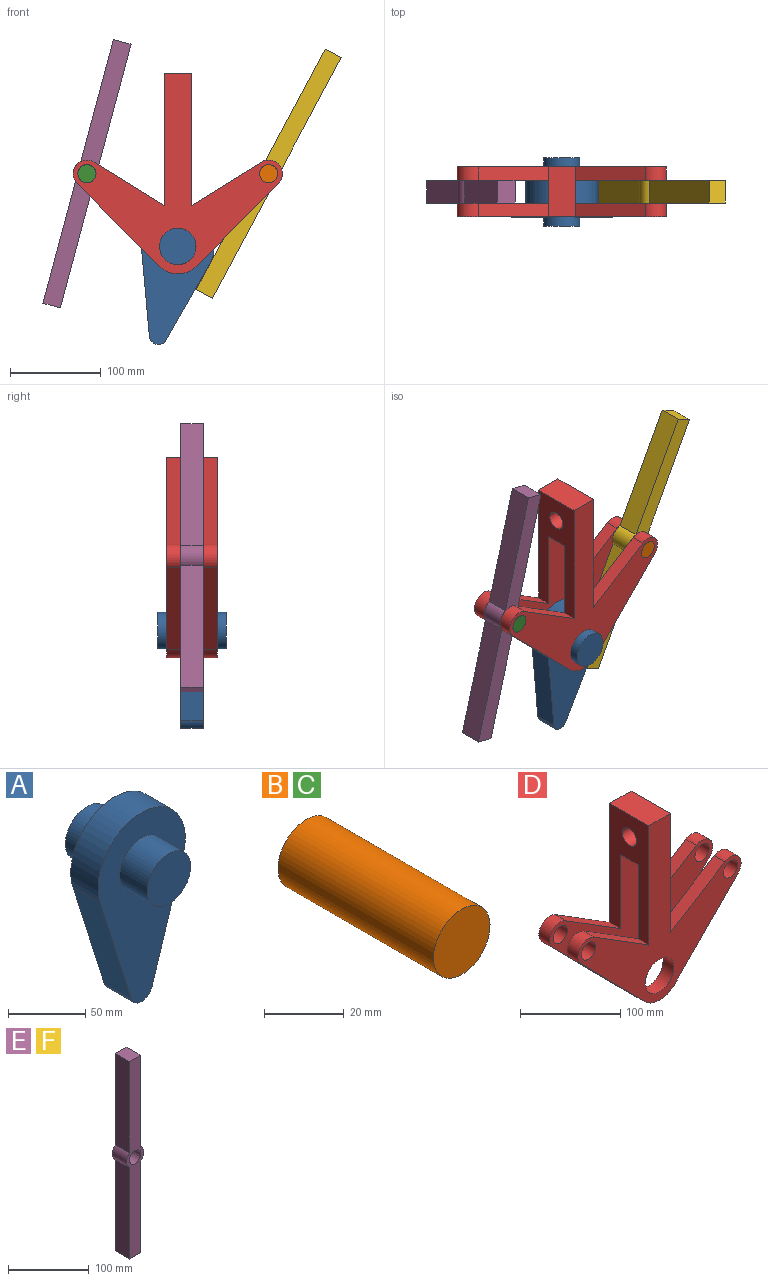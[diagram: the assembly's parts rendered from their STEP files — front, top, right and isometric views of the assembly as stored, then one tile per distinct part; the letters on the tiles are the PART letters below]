
ASSEMBLY  parts=6 mates=5
PART A: 10 faces, bbox 80x75x150 mm
  f0: cylinder r=10mm len=25mm, axis (0,1,0), area 633.1mm2, adj f1,f3,f4,f5
  f1: plane 91x28.62mm, normal (0.95,0,-0.3), area 2384.8mm2, adj f0,f2,f4,f5
  f2: cylinder r=40mm len=80mm, axis (0,1,0), area 3751mm2, adj f1,f3,f4,f5
  f3: plane 91x28.62mm, normal (-0.95,0,-0.3), area 2384.8mm2, adj f0,f2,f4,f5
  f4: plane 150x80mm, normal (0,-1,0), area 6640.5mm2, adj f0,f1,f2,f3,f8
  f5: plane 150x80mm, normal (0,1,0), area 6640.5mm2, adj f0,f1,f2,f3,f7
  f6: plane 40x40mm, normal (0,1,0), area 1256.6mm2, adj f7
  f7: cylinder r=20mm len=40mm, axis (0,1,0), area 3141.6mm2, adj f5,f6
  f8: cylinder r=20mm len=40mm, axis (0,1,0), area 3141.6mm2, adj f4,f9
  f9: plane 40x40mm, normal (0,-1,0), area 1256.6mm2, adj f8
PART B: 3 faces, bbox 20x55x20 mm
  f0: cylinder r=10mm len=55mm, axis (0,1,0), area 3455.8mm2, adj f1,f2
  f1: plane 20x20mm, normal (0,-1,0), area 314.2mm2, adj f0
  f2: plane 20x20mm, normal (0,1,0), area 314.2mm2, adj f0
PART C: same geometry as B
PART D: 29 faces, bbox 229.7x55x220 mm
  f0: plane 90.45x89.19mm, normal (-0.71,0,-0.7), area 1905.4mm2, adj f2,f20,f23,f26
  f1: plane 90.45x89.19mm, normal (-0.71,0,-0.7), area 1905.4mm2, adj f3,f21,f24,f27
  f2: cylinder r=30mm len=42.72mm, axis (0,1,0), area 713.2mm2, adj f0,f4,f23,f26
  f3: cylinder r=30mm len=42.72mm, axis (0,1,0), area 713.2mm2, adj f1,f5,f24,f27
  f4: plane 90.45x89.19mm, normal (0.71,0,-0.7), area 1905.4mm2, adj f2,f6,f23,f26
  f5: plane 90.45x89.19mm, normal (0.71,0,-0.7), area 1905.4mm2, adj f3,f7,f24,f27
  f6: cylinder r=15mm len=25.53mm, axis (0,1,0), area 654mm2, adj f4,f8,f23,f26
  f7: cylinder r=15mm len=25.53mm, axis (0,1,0), area 654mm2, adj f5,f9,f24,f27
  f8: plane 76.93x47.95mm, normal (-0.53,0,0.85), area 1359.8mm2, adj f6,f10,f23,f26
  f9: plane 76.93x47.95mm, normal (-0.53,0,0.85), area 1359.8mm2, adj f7,f10,f24,f27
  f10: plane 145.3x55mm, normal (1,0,0), area 5419.9mm2, adj f8,f9,f22,f23,f24,f25,f26,f27
  f11: plane 145.3x55mm, normal (-1,0,0), area 5419.9mm2, adj f12,f13,f22,f23,f24,f25,f26,f27
  f12: plane 76.93x47.95mm, normal (0.53,0,0.85), area 1359.8mm2, adj f11,f20,f23,f26
  f13: plane 76.93x47.95mm, normal (0.53,0,0.85), area 1359.8mm2, adj f11,f21,f24,f27
  f14: cylinder r=20mm len=40mm, axis (0,1,0), area 1885mm2, adj f23,f26
  f15: cylinder r=20mm len=40mm, axis (0,1,0), area 1885mm2, adj f24,f27
  f16: cylinder r=10mm len=20mm, axis (0,1,0), area 942.5mm2, adj f23,f26
  f17: cylinder r=10mm len=20mm, axis (0,1,0), area 942.5mm2, adj f24,f27
  f18: cylinder r=10mm len=20mm, axis (0,1,0), area 942.5mm2, adj f23,f26
  f19: cylinder r=10mm len=20mm, axis (0,1,0), area 942.5mm2, adj f24,f27
  f20: cylinder r=15mm len=25.53mm, axis (0,1,0), area 654mm2, adj f0,f12,f23,f26
  f21: cylinder r=15mm len=25.53mm, axis (0,1,0), area 654mm2, adj f1,f13,f24,f27
  f22: plane 55x30mm, normal (0,0,1), area 1650mm2, adj f10,f11,f23,f24
  f23: plane 229.74x220mm, normal (0,-1,0), area 14852.9mm2, adj f0,f2,f4,f6,f8,f10,f11,f12
  f24: plane 229.74x220mm, normal (0,1,0), area 14852.9mm2, adj f1,f3,f5,f7,f9,f10,f11,f13
  f25: cylinder r=10mm len=30mm, axis (-1,0,0), area 1885mm2, adj f10,f11
  f26: plane 229.74x165mm, normal (0,1,0), area 13202.9mm2, adj f0,f2,f4,f6,f8,f10,f11,f12
  f27: plane 229.74x165mm, normal (0,-1,0), area 13202.9mm2, adj f1,f3,f5,f7,f9,f10,f11,f13
  f28: plane 30x25mm, normal (0,0,-1), area 750mm2, adj f10,f11,f26,f27
PART E: 11 faces, bbox 30x25x300 mm
  f0: plane 138.82x25mm, normal (-1,0,0), area 3470.5mm2, adj f1,f8,f9,f10
  f1: cylinder r=15mm len=25mm, axis (0,1,0), area 630.8mm2, adj f0,f2,f9,f10
  f2: plane 138.82x25mm, normal (-1,0,0), area 3470.5mm2, adj f1,f3,f9,f10
  f3: plane 25x20mm, normal (0,0,-1), area 500mm2, adj f2,f4,f9,f10
  f4: plane 138.82x25mm, normal (1,0,0), area 3470.5mm2, adj f3,f5,f9,f10
  f5: cylinder r=15mm len=25mm, axis (0,1,0), area 630.8mm2, adj f4,f6,f9,f10
  f6: plane 138.82x25mm, normal (1,0,0), area 3470.5mm2, adj f5,f8,f9,f10
  f7: cylinder r=10mm len=25mm, axis (0,1,0), area 1570.8mm2, adj f9,f10
  f8: plane 25x20mm, normal (0,0,1), area 500mm2, adj f0,f6,f9,f10
  f9: plane 300x30mm, normal (0,-1,0), area 5840.7mm2, adj f0,f1,f2,f3,f4,f5,f6,f7
  f10: plane 300x30mm, normal (0,1,0), area 5840.7mm2, adj f0,f1,f2,f3,f4,f5,f6,f7
PART F: same geometry as E
PLACE A rot(axis=(0,1,0),12.3deg) t=(-169.39,-137.45,-148.46)mm
PLACE B rot(axis=(0,1,0),28.2deg) t=(-69.52,-109.95,-68.55)mm
PLACE C rot(axis=(0,1,0),15deg) t=(-269.26,-109.95,-68.55)mm
PLACE D t=(-169.39,-109.95,-148.46)mm
PLACE E rot(axis=(0,1,0),15deg) t=(-269.26,-124.95,-68.55)mm
PLACE F rot(axis=(0,1,0),28.2deg) t=(-69.52,-124.95,-68.55)mm
MATE revolute B.f0 <-> D.f6  axis (0,1,0) through (-69.52,-109.95,-68.55)mm
MATE revolute A.f7 <-> D.f14  axis (0,-1,0) through (-169.39,-149.95,-148.46)mm
MATE revolute C.f0 <-> D.f16  axis (0,1,0) through (-269.26,-109.95,-68.55)mm
MATE fastened C.f0 <-> E.f7  axis (0,1,0) through (-269.26,-137.45,-68.55)mm
MATE fastened B.f0 <-> F.f7  axis (0,1,0) through (-69.52,-137.45,-68.55)mm
